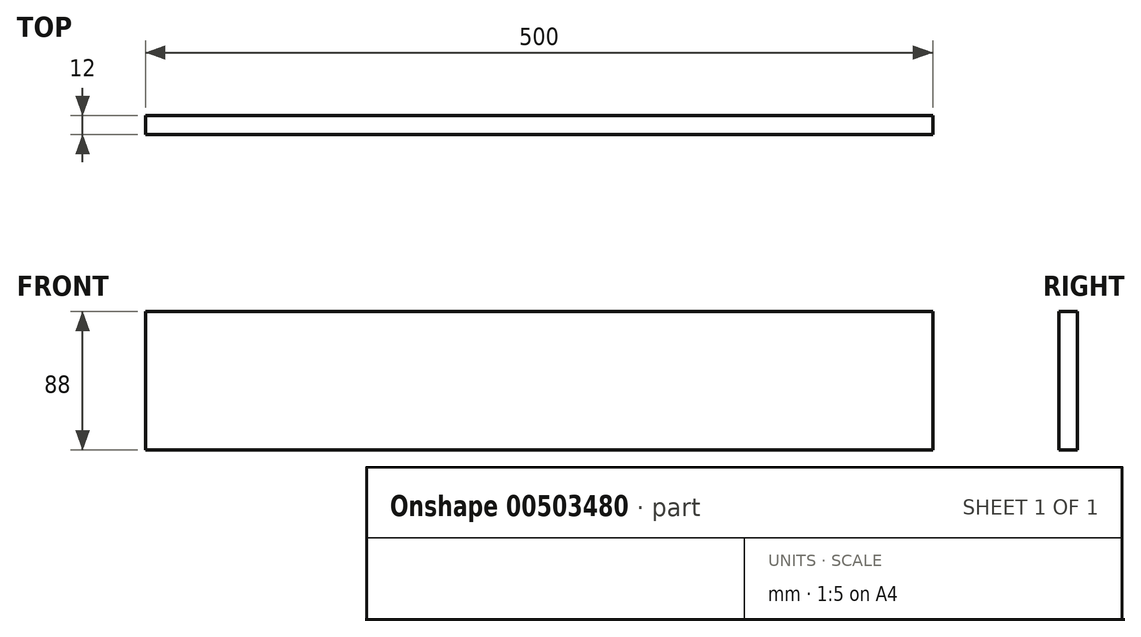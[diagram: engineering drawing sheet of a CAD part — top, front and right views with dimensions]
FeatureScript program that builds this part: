
annotation { "Feature Type Name" : "Feature", "Feature Type Description" : "" }
export const myFeature = defineFeature(function(context is Context, id is Id, definition is map)
    precondition{}
    {
        {
            var Q0;
            Q0=qCreatedBy(makeId("Top.planeOp"),FACE);
            var sketch = newSketch(context, id + "F0", { "sketchPlane" : qUnion([Q0])});
            skLineSegment(sketch, "E0.bottom", {"start": v(250, -250) * mm, "end": v(-250, -250) * mm});
            skLineSegment(sketch, "E0.top", {"start": v(250, 250) * mm, "end": v(-250, 250) * mm});
            skLineSegment(sketch, "E0.left", {"start": v(250, -250) * mm, "end": v(250, 250) * mm});
            skLineSegment(sketch, "E0.right", {"start": v(-250, -250) * mm, "end": v(-250, 250) * mm});
            skPoint(sketch, "E0.middle", {"position": v(0, 0) * mm});
            skSolve(sketch);
        }
        {
            var Q0;
            Q0=qSketchRegion(id+"F0",true);
            extrude(context, id + "F1", {"entities" : qUnion([Q0]), "depth" : 12 * mm, "offsetDistance" : 25 * mm});
        }
        {
            var Q0;
            Q0=qCreatedBy(makeId("Right.planeOp"),FACE);
            var sketch = newSketch(context, id + "F2", { "sketchPlane" : qUnion([Q0])});
            skLineSegment(sketch, "E1.bottom", {"start": v(250, -25) * mm, "end": v(-250, -25) * mm});
            skLineSegment(sketch, "E1.top", {"start": v(250, 25) * mm, "end": v(-250, 25) * mm});
            skLineSegment(sketch, "E1.left", {"start": v(250, -25) * mm, "end": v(250, 25) * mm});
            skLineSegment(sketch, "E1.right", {"start": v(-250, -25) * mm, "end": v(-250, 25) * mm});
            skPoint(sketch, "E1.middle", {"position": v(0, 0) * mm});
            skSolve(sketch);
        }
        {
            var Q0;
            Q0=qSketchRegion(id+"F2",true);
            extrude(context, id + "F3", {"entities" : qUnion([Q0]), "endBound" : BoundingType.SYMMETRIC, "depth" : 12 * mm, "offsetDistance" : 25 * mm});
        }
        {
            var Q0;
            Q0=makeQuery(id+"F3.opExtrude","SWEPT_BODY",BODY,{"disambiguationData":[OSD([sQuery(id+"F2.wireOp",EDGE,"E1.bottom"),sQuery(id+"F2.wireOp",EDGE,"E1.top"),sQuery(id+"F2.wireOp",EDGE,"E1.left"),sQuery(id+"F2.wireOp",EDGE,"E1.right")])]});
            transform(context, id + "F4", {"entities" : qUnion([Q0]), "transformType" : TransformType.TRANSLATION_3D, "dx" : 0 * mm, "dy" : 0 * mm, "dz" : -25 * mm, "makeCopy" : false});
        }
        {
            var Q0;
            Q0=qCreatedBy(makeId("Front.planeOp"),FACE);
            var sketch = newSketch(context, id + "F5", { "sketchPlane" : qUnion([Q0])});
            skLineSegment(sketch, "E2.bottom", {"start": v(250, -25) * mm, "end": v(-250, -25) * mm});
            skLineSegment(sketch, "E2.left", {"start": v(250, -25) * mm, "end": v(250, 25) * mm});
            skLineSegment(sketch, "E2.right", {"start": v(-250, -25) * mm, "end": v(-250, 25) * mm});
            skPoint(sketch, "E2.middle", {"position": v(0, 0) * mm});
            skLineSegment(sketch, "E3", {"start": v(-250, 25) * mm, "end": v(-6, 25) * mm});
            skLineSegment(sketch, "E4", {"start": v(-6, 25) * mm, "end": v(-6, 0) * mm});
            skLineSegment(sketch, "E5", {"start": v(-6, 0) * mm, "end": v(6, 0) * mm});
            skLineSegment(sketch, "E6", {"start": v(6, 0) * mm, "end": v(6, 25) * mm});
            skLineSegment(sketch, "E7", {"start": v(6, 25) * mm, "end": v(250, 25) * mm});
            skSolve(sketch);
        }
        {
            var Q0;
            Q0=qSketchRegion(id+"F5",true);
            extrude(context, id + "F6", {"entities" : qUnion([Q0]), "endBound" : BoundingType.SYMMETRIC, "depth" : 12 * mm, "offsetDistance" : 25 * mm});
        }
        {
            var Q0;
            Q0=makeQuery(id+"F6.opExtrude","SWEPT_BODY",BODY,{"disambiguationData":[OSD([sQuery(id+"F5.wireOp",EDGE,"E2.bottom"),sQuery(id+"F5.wireOp",EDGE,"E2.top"),sQuery(id+"F5.wireOp",EDGE,"E2.left"),sQuery(id+"F5.wireOp",EDGE,"E2.right")])]});
            transform(context, id + "F7", {"entities" : qUnion([Q0]), "transformType" : TransformType.TRANSLATION_3D, "dx" : 0 * mm, "dy" : 80 * mm, "dz" : -25 * mm, "makeCopy" : false});
        }
        {
            var Q0;
            Q0=makeQuery(id+"F6.opExtrude","SWEPT_BODY",BODY,{"disambiguationData":[OSD([sQuery(id+"F5.wireOp",EDGE,"E2.bottom"),sQuery(id+"F5.wireOp",EDGE,"E2.top"),sQuery(id+"F5.wireOp",EDGE,"E2.left"),sQuery(id+"F5.wireOp",EDGE,"E2.right")])]});
            transform(context, id + "F8", {"entities" : qUnion([Q0]), "transformType" : TransformType.COPY});
        }
        {
            var Q0;
            Q0=makeQuery(id+"F8.opPattern","COPY",BODY,{"derivedFrom":makeQuery(id+"F6.opExtrude","SWEPT_BODY",BODY,{"disambiguationData":[OSD([sQuery(id+"F5.wireOp",EDGE,"E2.bottom"),sQuery(id+"F5.wireOp",EDGE,"E2.top"),sQuery(id+"F5.wireOp",EDGE,"E2.left"),sQuery(id+"F5.wireOp",EDGE,"E2.right")])]}),"instanceName":"1"});
            deleteBodies(context, id + "F9", {"entities" : qUnion([Q0])});
        }
        {
            var Q0;
            Q0=makeQuery(id+"F6.opExtrude","SWEPT_BODY",BODY,{"disambiguationData":[OSD([sQuery(id+"F5.wireOp",EDGE,"E2.bottom"),sQuery(id+"F5.wireOp",EDGE,"E2.left"),sQuery(id+"F5.wireOp",EDGE,"E2.right"),sQuery(id+"F5.wireOp",EDGE,"E3"),sQuery(id+"F5.wireOp",EDGE,"E4"),sQuery(id+"F5.wireOp",EDGE,"E5"),sQuery(id+"F5.wireOp",EDGE,"E6"),sQuery(id+"F5.wireOp",EDGE,"E7")])]});
            var Q1;
            Q1=makeQuery(id+"F3.opExtrude","SWEPT_BODY",BODY,{"disambiguationData":[OSD([sQuery(id+"F2.wireOp",EDGE,"E1.bottom"),sQuery(id+"F2.wireOp",EDGE,"E1.top"),sQuery(id+"F2.wireOp",EDGE,"E1.left"),sQuery(id+"F2.wireOp",EDGE,"E1.right")])]});
            booleanBodies(context, id + "F10", {"operationType" : BooleanOperationType.SUBTRACTION, "tools" : qUnion([Q0]), "targets" : qUnion([Q1]), "keepTools" : true});
        }
        {
            var Q0;
            Q0=makeQuery(id+"F6.opExtrude","SWEPT_BODY",BODY,{"disambiguationData":[OSD([sQuery(id+"F5.wireOp",EDGE,"E2.bottom"),sQuery(id+"F5.wireOp",EDGE,"E2.left"),sQuery(id+"F5.wireOp",EDGE,"E2.right"),sQuery(id+"F5.wireOp",EDGE,"E3"),sQuery(id+"F5.wireOp",EDGE,"E4"),sQuery(id+"F5.wireOp",EDGE,"E5"),sQuery(id+"F5.wireOp",EDGE,"E6"),sQuery(id+"F5.wireOp",EDGE,"E7")])]});
            transform(context, id + "F11", {"entities" : qUnion([Q0]), "transformType" : TransformType.TRANSLATION_3D, "dx" : 0 * mm, "dy" : 164 * mm, "dz" : 0 * mm, "makeCopy" : true});
        }
        {
            var Q0;
            Q0=makeQuery(id+"F11.opPattern","COPY",BODY,{"derivedFrom":makeQuery(id+"F6.opExtrude","SWEPT_BODY",BODY,{"disambiguationData":[OSD([sQuery(id+"F5.wireOp",EDGE,"E2.bottom"),sQuery(id+"F5.wireOp",EDGE,"E2.left"),sQuery(id+"F5.wireOp",EDGE,"E2.right"),sQuery(id+"F5.wireOp",EDGE,"E3"),sQuery(id+"F5.wireOp",EDGE,"E4"),sQuery(id+"F5.wireOp",EDGE,"E5"),sQuery(id+"F5.wireOp",EDGE,"E6"),sQuery(id+"F5.wireOp",EDGE,"E7")])]}),"instanceName":"1"});
            var Q1;
            Q1=makeQuery(id+"F3.opExtrude","SWEPT_BODY",BODY,{"disambiguationData":[OSD([sQuery(id+"F2.wireOp",EDGE,"E1.bottom"),sQuery(id+"F2.wireOp",EDGE,"E1.top"),sQuery(id+"F2.wireOp",EDGE,"E1.left"),sQuery(id+"F2.wireOp",EDGE,"E1.right")])]});
            booleanBodies(context, id + "F12", {"operationType" : BooleanOperationType.SUBTRACTION, "tools" : qUnion([Q0]), "targets" : qUnion([Q1]), "keepTools" : true});
        }
        {
            var Q0;
            Q0=qCreatedBy(makeId("Right.planeOp"),FACE);
            var sketch = newSketch(context, id + "F13", { "sketchPlane" : qUnion([Q0])});
            skLineSegment(sketch, "E8", {"start": v(0, 0) * mm, "end": v(250, 0) * mm});
            skLineSegment(sketch, "E9", {"start": v(250, 0) * mm, "end": v(250, -50) * mm});
            skLineSegment(sketch, "E10", {"start": v(250, -50) * mm, "end": v(-250, -50) * mm});
            skLineSegment(sketch, "E11", {"start": v(-250, -50) * mm, "end": v(-250, 100) * mm});
            skLineSegment(sketch, "E12", {"start": v(250, 0) * mm, "end": v(250, 452) * mm});
            skLineSegment(sketch, "E13", {"start": v(250, 452) * mm, "end": v(-110, 452) * mm});
            skLineSegment(sketch, "E14", {"start": v(-110, 452) * mm, "end": v(-250, 100) * mm});
            skLineSegment(sketch, "E15", {"start": v(250, 452) * mm, "end": v(70, 452) * mm});
            skLineSegment(sketch, "E16", {"start": v(70, 452) * mm, "end": v(70, 392) * mm});
            skLineSegment(sketch, "E17.bottom", {"start": v(140, 372) * mm, "end": v(0, 372) * mm});
            skLineSegment(sketch, "E17.top", {"start": v(140, 412) * mm, "end": v(0, 412) * mm});
            skLineSegment(sketch, "E17.left", {"start": v(140, 372) * mm, "end": v(140, 412) * mm});
            skLineSegment(sketch, "E17.right", {"start": v(0, 372) * mm, "end": v(0, 412) * mm});
            skPoint(sketch, "E17.middle", {"position": v(70, 392) * mm});
            skSolve(sketch);
        }
        {
            var Q0;
            Q0=makeQuery(id+"F13.imprint","IMPRINT",FACE,{"disambiguationData":[TD([[makeQuery(id+"F13.imprint","IMPRINT",EDGE,{"derivedFrom":sQuery(id+"F13.wireOp",EDGE,"E9")}),-1.0]])]});
            extrude(context, id + "F14", {"entities" : qUnion([Q0]), "endBound" : BoundingType.SYMMETRIC, "depth" : 12 * mm, "offsetDistance" : 25 * mm});
        }
        {
            var Q0;
            Q0=makeQuery(id+"F14.opExtrude","SWEPT_EDGE",EDGE,{"disambiguationData":[OSD([sQuery(id+"F13.wireOp",EDGE,"E17.bottom"),sQuery(id+"F13.wireOp",EDGE,"E17.left")])]});
            var Q1;
            Q1=makeQuery(id+"F14.opExtrude","SWEPT_EDGE",EDGE,{"disambiguationData":[OSD([sQuery(id+"F13.wireOp",EDGE,"E17.top"),sQuery(id+"F13.wireOp",EDGE,"E17.left")])]});
            var Q2;
            Q2=makeQuery(id+"F14.opExtrude","SWEPT_EDGE",EDGE,{"disambiguationData":[OSD([sQuery(id+"F13.wireOp",EDGE,"E17.top"),sQuery(id+"F13.wireOp",EDGE,"E17.right")])]});
            var Q3;
            Q3=makeQuery(id+"F14.opExtrude","SWEPT_EDGE",EDGE,{"disambiguationData":[OSD([sQuery(id+"F13.wireOp",EDGE,"E17.bottom"),sQuery(id+"F13.wireOp",EDGE,"E17.right")])]});
            fillet(context, id + "F15", {"entities" : qUnion([Q0, Q1, Q2, Q3]), "radius" : 20 * mm, "tangentPropagation" : true, "allowEdgeOverflow" : false});
        }
        {
            var Q0;
            Q0=makeQuery(id+"F14.opExtrude","SWEPT_BODY",BODY,{"disambiguationData":[OSD([sQuery(id+"F13.wireOp",EDGE,"E9"),sQuery(id+"F13.wireOp",EDGE,"E10"),sQuery(id+"F13.wireOp",EDGE,"E11"),sQuery(id+"F13.wireOp",EDGE,"E12"),sQuery(id+"F13.wireOp",EDGE,"E13"),sQuery(id+"F13.wireOp",EDGE,"E14"),sQuery(id+"F13.wireOp",EDGE,"E17.bottom"),sQuery(id+"F13.wireOp",EDGE,"E17.top"),sQuery(id+"F13.wireOp",EDGE,"E17.left"),sQuery(id+"F13.wireOp",EDGE,"E17.right")])]});
            transform(context, id + "F16", {"entities" : qUnion([Q0]), "transformType" : TransformType.TRANSLATION_3D, "dx" : -256 * mm, "dy" : 0 * mm, "dz" : 0 * mm, "makeCopy" : false});
        }
        {
            var Q0;
            Q0=makeQuery(id+"F14.opExtrude","SWEPT_BODY",BODY,{"disambiguationData":[OSD([sQuery(id+"F13.wireOp",EDGE,"E9"),sQuery(id+"F13.wireOp",EDGE,"E10"),sQuery(id+"F13.wireOp",EDGE,"E11"),sQuery(id+"F13.wireOp",EDGE,"E12"),sQuery(id+"F13.wireOp",EDGE,"E13"),sQuery(id+"F13.wireOp",EDGE,"E14"),sQuery(id+"F13.wireOp",EDGE,"E17.bottom"),sQuery(id+"F13.wireOp",EDGE,"E17.top"),sQuery(id+"F13.wireOp",EDGE,"E17.left"),sQuery(id+"F13.wireOp",EDGE,"E17.right")])]});
            transform(context, id + "F17", {"entities" : qUnion([Q0]), "transformType" : TransformType.TRANSLATION_3D, "dx" : 512 * mm, "dy" : 0 * mm, "dz" : 0 * mm, "makeCopy" : true});
        }
        {
            var Q0;
            Q0=qCreatedBy(makeId("Front.planeOp"),FACE);
            var sketch = newSketch(context, id + "F18", { "sketchPlane" : qUnion([Q0])});
            skLineSegment(sketch, "E18", {"start": v(0, 0) * mm, "end": v(-262, 0) * mm});
            skLineSegment(sketch, "E19", {"start": v(-262, 0) * mm, "end": v(-262, -50) * mm});
            skLineSegment(sketch, "E20", {"start": v(-262, -50) * mm, "end": v(262, -50) * mm});
            skLineSegment(sketch, "E21", {"start": v(262, -50) * mm, "end": v(262, 452) * mm});
            skLineSegment(sketch, "E22", {"start": v(262, 452) * mm, "end": v(-262, 452) * mm});
            skLineSegment(sketch, "E23", {"start": v(-262, 452) * mm, "end": v(-262, 0) * mm});
            skSolve(sketch);
        }
        {
            var Q0;
            Q0=qSketchRegion(id+"F18",true);
            extrude(context, id + "F19", {"entities" : qUnion([Q0]), "endBound" : BoundingType.SYMMETRIC, "depth" : 12 * mm, "offsetDistance" : 25 * mm});
        }
        {
            var Q0;
            Q0=makeQuery(id+"F19.opExtrude","SWEPT_BODY",BODY,{"disambiguationData":[OSD([sQuery(id+"F18.wireOp",EDGE,"E19"),sQuery(id+"F18.wireOp",EDGE,"E20"),sQuery(id+"F18.wireOp",EDGE,"E21"),sQuery(id+"F18.wireOp",EDGE,"E22"),sQuery(id+"F18.wireOp",EDGE,"E23")])]});
            transform(context, id + "F20", {"entities" : qUnion([Q0]), "transformType" : TransformType.TRANSLATION_3D, "dx" : 0 * mm, "dy" : 256 * mm, "dz" : 0 * mm, "makeCopy" : false});
        }
        {
            var Q0;
            Q0=makeQuery(id+"F1.opExtrude","CAP_FACE",FACE,{"disambiguationData":[OSD([sQuery(id+"F0.wireOp",EDGE,"E0.bottom"),sQuery(id+"F0.wireOp",EDGE,"E0.top"),sQuery(id+"F0.wireOp",EDGE,"E0.left"),sQuery(id+"F0.wireOp",EDGE,"E0.right")])],"isStart":false});
            var sketch = newSketch(context, id + "F21", { "sketchPlane" : qUnion([Q0])});
            skLineSegment(sketch, "E24", {"start": v(0, 0) * mm, "end": v(0, 262) * mm});
            skLineSegment(sketch, "E25", {"start": v(0, 262) * mm, "end": v(262, 262) * mm});
            skLineSegment(sketch, "E26", {"start": v(262, 262) * mm, "end": v(262, -110) * mm});
            skLineSegment(sketch, "E27", {"start": v(262, -110) * mm, "end": v(-262, -110) * mm});
            skLineSegment(sketch, "E28", {"start": v(-262, -110) * mm, "end": v(-262, 262) * mm});
            skLineSegment(sketch, "E29", {"start": v(-262, 262) * mm, "end": v(0, 262) * mm});
            skSolve(sketch);
        }
        {
            var Q0;
            Q0=qSketchRegion(id+"F21",true);
            extrude(context, id + "F22", {"entities" : qUnion([Q0]), "depth" : 12 * mm, "offsetDistance" : 25 * mm});
        }
        {
            var Q0;
            Q0=makeQuery(id+"F22.opExtrude","SWEPT_BODY",BODY,{"disambiguationData":[OSD([sQuery(id+"F21.wireOp",EDGE,"E25"),sQuery(id+"F21.wireOp",EDGE,"E26"),sQuery(id+"F21.wireOp",EDGE,"E27"),sQuery(id+"F21.wireOp",EDGE,"E28"),sQuery(id+"F21.wireOp",EDGE,"E29")])]});
            transform(context, id + "F23", {"entities" : qUnion([Q0]), "transformType" : TransformType.TRANSLATION_3D, "dx" : 0 * mm, "dy" : 0 * mm, "dz" : 440 * mm, "makeCopy" : false});
        }
        {
            var Q0;
            Q0=qCreatedBy(makeId("Front.planeOp"),FACE);
            var sketch = newSketch(context, id + "F24", { "sketchPlane" : qUnion([Q0])});
            skLineSegment(sketch, "E30", {"start": v(0, 0) * mm, "end": v(0, 12) * mm});
            skLineSegment(sketch, "E31", {"start": v(0, 12) * mm, "end": v(250, 12) * mm});
            skLineSegment(sketch, "E32", {"start": v(250, 12) * mm, "end": v(250, 100) * mm});
            skLineSegment(sketch, "E33", {"start": v(250, 100) * mm, "end": v(-250, 100) * mm});
            skLineSegment(sketch, "E34", {"start": v(-250, 100) * mm, "end": v(-250, 12) * mm});
            skLineSegment(sketch, "E35", {"start": v(-250, 12) * mm, "end": v(0, 12) * mm});
            skSolve(sketch);
        }
        {
            var Q0;
            Q0=qSketchRegion(id+"F24",true);
            extrude(context, id + "F25", {"entities" : qUnion([Q0]), "endBound" : BoundingType.SYMMETRIC, "depth" : 12 * mm, "offsetDistance" : 25 * mm});
        }
        {
            var Q0;
            Q0=makeQuery(id+"F25.opExtrude","SWEPT_BODY",BODY,{"disambiguationData":[OSD([sQuery(id+"F24.wireOp",EDGE,"E31"),sQuery(id+"F24.wireOp",EDGE,"E32"),sQuery(id+"F24.wireOp",EDGE,"E33"),sQuery(id+"F24.wireOp",EDGE,"E34"),sQuery(id+"F24.wireOp",EDGE,"E35")])]});
            transform(context, id + "F26", {"entities" : qUnion([Q0]), "transformType" : TransformType.TRANSLATION_3D, "dx" : 0 * mm, "dy" : -244 * mm, "dz" : 0 * mm, "makeCopy" : false});
        }
        {
            var Q0;
            Q0=qCreatedBy(makeId("Top.planeOp"),FACE);
            var sketch = newSketch(context, id + "F27", { "sketchPlane" : qUnion([Q0])});
            skLineSegment(sketch, "E36", {"start": v(0, 0) * mm, "end": v(0, 70) * mm});
            skLineSegment(sketch, "E37", {"start": v(0, 70) * mm, "end": v(-18, 70) * mm});
            skLineSegment(sketch, "E38", {"start": v(-18, 70) * mm, "end": v(-18, -250) * mm});
            skLineSegment(sketch, "E39", {"start": v(-18, -250) * mm, "end": v(-30, -250) * mm});
            skLineSegment(sketch, "E40", {"start": v(-30, -250) * mm, "end": v(-30, 70) * mm});
            skLineSegment(sketch, "E41", {"start": v(-30, 70) * mm, "end": v(-18, 70) * mm});
            skSolve(sketch);
        }
        {
            var Q0;
            Q0=qSketchRegion(id+"F27",true);
            extrude(context, id + "F28", {"entities" : qUnion([Q0]), "depth" : 44 * mm, "offsetDistance" : 25 * mm});
        }
        {
            var Q0;
            Q0=makeQuery(id+"F28.opExtrude","SWEPT_BODY",BODY,{"disambiguationData":[OSD([sQuery(id+"F27.wireOp",EDGE,"E38"),sQuery(id+"F27.wireOp",EDGE,"E39"),sQuery(id+"F27.wireOp",EDGE,"E40"),sQuery(id+"F27.wireOp",EDGE,"E41")])]});
            transform(context, id + "F29", {"entities" : qUnion([Q0]), "transformType" : TransformType.TRANSLATION_3D, "dx" : 0 * mm, "dy" : 0 * mm, "dz" : -48 * mm, "makeCopy" : false});
        }
        {
            var Q0;
            Q0=makeQuery(id+"F28.opExtrude","SWEPT_BODY",BODY,{"disambiguationData":[OSD([sQuery(id+"F27.wireOp",EDGE,"E38"),sQuery(id+"F27.wireOp",EDGE,"E39"),sQuery(id+"F27.wireOp",EDGE,"E40"),sQuery(id+"F27.wireOp",EDGE,"E41")])]});
            transform(context, id + "F30", {"entities" : qUnion([Q0]), "transformType" : TransformType.TRANSLATION_3D, "dx" : -208 * mm, "dy" : 0 * mm, "dz" : 0 * mm, "makeCopy" : true});
        }
        {
            var Q0;
            Q0=qCreatedBy(makeId("Top.planeOp"),FACE);
            var sketch = newSketch(context, id + "F31", { "sketchPlane" : qUnion([Q0])});
            skLineSegment(sketch, "E42", {"start": v(0, 0) * mm, "end": v(0, -250) * mm});
            skLineSegment(sketch, "E43", {"start": v(0, -250) * mm, "end": v(-30, -250) * mm});
            skLineSegment(sketch, "E44", {"start": v(-30, -250) * mm, "end": v(-226, -250) * mm});
            skLineSegment(sketch, "E45", {"start": v(-226, -250) * mm, "end": v(-226, -238) * mm});
            skLineSegment(sketch, "E46", {"start": v(-226, -238) * mm, "end": v(-30, -238) * mm});
            skLineSegment(sketch, "E47", {"start": v(-30, -238) * mm, "end": v(-30, -250) * mm});
            skSolve(sketch);
        }
        {
            var Q0;
            Q0=qSketchRegion(id+"F31",true);
            extrude(context, id + "F32", {"entities" : qUnion([Q0]), "depth" : -44 * mm, "offsetDistance" : 25 * mm});
        }
        {
            var Q0;
            Q0=makeQuery(id+"F32.opExtrude","SWEPT_BODY",BODY,{"disambiguationData":[OSD([sQuery(id+"F31.wireOp",EDGE,"E44"),sQuery(id+"F31.wireOp",EDGE,"E45"),sQuery(id+"F31.wireOp",EDGE,"E46"),sQuery(id+"F31.wireOp",EDGE,"E47")])]});
            transform(context, id + "F33", {"entities" : qUnion([Q0]), "transformType" : TransformType.TRANSLATION_3D, "dx" : 0 * mm, "dy" : 0 * mm, "dz" : -4 * mm, "makeCopy" : false});
        }
        {
            var Q0;
            Q0=makeQuery(id+"F32.opExtrude","SWEPT_BODY",BODY,{"disambiguationData":[OSD([sQuery(id+"F31.wireOp",EDGE,"E44"),sQuery(id+"F31.wireOp",EDGE,"E45"),sQuery(id+"F31.wireOp",EDGE,"E46"),sQuery(id+"F31.wireOp",EDGE,"E47")])]});
            transform(context, id + "F34", {"entities" : qUnion([Q0]), "transformType" : TransformType.TRANSLATION_3D, "dx" : 0 * mm, "dy" : 308 * mm, "dz" : 0 * mm, "makeCopy" : true});
        }
        {
            var Q0;
            Q0=makeQuery(id+"F32.opExtrude","SWEPT_BODY",BODY,{"disambiguationData":[OSD([sQuery(id+"F31.wireOp",EDGE,"E44"),sQuery(id+"F31.wireOp",EDGE,"E45"),sQuery(id+"F31.wireOp",EDGE,"E46"),sQuery(id+"F31.wireOp",EDGE,"E47")])]});
            var Q1;
            Q1=makeQuery(id+"F30.opPattern","COPY",BODY,{"derivedFrom":makeQuery(id+"F28.opExtrude","SWEPT_BODY",BODY,{"disambiguationData":[OSD([sQuery(id+"F27.wireOp",EDGE,"E38"),sQuery(id+"F27.wireOp",EDGE,"E39"),sQuery(id+"F27.wireOp",EDGE,"E40"),sQuery(id+"F27.wireOp",EDGE,"E41")])]}),"instanceName":"1"});
            var Q2;
            Q2=makeQuery(id+"F28.opExtrude","SWEPT_BODY",BODY,{"disambiguationData":[OSD([sQuery(id+"F27.wireOp",EDGE,"E38"),sQuery(id+"F27.wireOp",EDGE,"E39"),sQuery(id+"F27.wireOp",EDGE,"E40"),sQuery(id+"F27.wireOp",EDGE,"E41")])]});
            var Q3;
            Q3=makeQuery(id+"F34.opPattern","COPY",BODY,{"derivedFrom":makeQuery(id+"F32.opExtrude","SWEPT_BODY",BODY,{"disambiguationData":[OSD([sQuery(id+"F31.wireOp",EDGE,"E44"),sQuery(id+"F31.wireOp",EDGE,"E45"),sQuery(id+"F31.wireOp",EDGE,"E46"),sQuery(id+"F31.wireOp",EDGE,"E47")])]}),"instanceName":"1"});
            transform(context, id + "F35", {"entities" : qUnion([Q0, Q1, Q2, Q3]), "transformType" : TransformType.TRANSLATION_3D, "dx" : 256 * mm, "dy" : 0 * mm, "dz" : 0 * mm, "makeCopy" : true});
        }
        {
            var Q0;
            Q0=qCreatedBy(makeId("Top.planeOp"),FACE);
            var sketch = newSketch(context, id + "F36", { "sketchPlane" : qUnion([Q0])});
            skLineSegment(sketch, "E48", {"start": v(0, 0) * mm, "end": v(-24, 0) * mm});
            skLineSegment(sketch, "E49", {"start": v(-24, 0) * mm, "end": v(-24, -244) * mm});
            skLineSegment(sketch, "E50", {"start": v(-24, -244) * mm, "end": v(-232, -244) * mm});
            skLineSegment(sketch, "E51", {"start": v(-232, -244) * mm, "end": v(-232, 64) * mm});
            skLineSegment(sketch, "E52", {"start": v(-232, 64) * mm, "end": v(-24, 64) * mm});
            skLineSegment(sketch, "E53", {"start": v(-24, 64) * mm, "end": v(-24, 0) * mm});
            skSolve(sketch);
        }
        {
            var Q0;
            Q0=qSketchRegion(id+"F36",true);
            extrude(context, id + "F37", {"entities" : qUnion([Q0]), "depth" : 3 * mm, "offsetDistance" : 25 * mm});
        }
        {
            var Q0;
            Q0=makeQuery(id+"F37.opExtrude","SWEPT_BODY",BODY,{"disambiguationData":[OSD([sQuery(id+"F36.wireOp",EDGE,"E49"),sQuery(id+"F36.wireOp",EDGE,"E50"),sQuery(id+"F36.wireOp",EDGE,"E51"),sQuery(id+"F36.wireOp",EDGE,"E52"),sQuery(id+"F36.wireOp",EDGE,"E53")])]});
            transform(context, id + "F38", {"entities" : qUnion([Q0]), "transformType" : TransformType.TRANSLATION_3D, "dx" : 0 * mm, "dy" : 0 * mm, "dz" : -44 * mm, "makeCopy" : false});
        }
        {
            var Q0;
            Q0=makeQuery(id+"F37.opExtrude","SWEPT_BODY",BODY,{"disambiguationData":[OSD([sQuery(id+"F36.wireOp",EDGE,"E49"),sQuery(id+"F36.wireOp",EDGE,"E50"),sQuery(id+"F36.wireOp",EDGE,"E51"),sQuery(id+"F36.wireOp",EDGE,"E52"),sQuery(id+"F36.wireOp",EDGE,"E53")])]});
            transform(context, id + "F39", {"entities" : qUnion([Q0]), "transformType" : TransformType.TRANSLATION_3D, "dx" : 256 * mm, "dy" : 0 * mm, "dz" : 0 * mm, "makeCopy" : true});
        }
        {
            var Q0;
            Q0=makeQuery(id+"F37.opExtrude","SWEPT_BODY",BODY,{"disambiguationData":[OSD([sQuery(id+"F36.wireOp",EDGE,"E49"),sQuery(id+"F36.wireOp",EDGE,"E50"),sQuery(id+"F36.wireOp",EDGE,"E51"),sQuery(id+"F36.wireOp",EDGE,"E52"),sQuery(id+"F36.wireOp",EDGE,"E53")])]});
            var Q1;
            Q1=makeQuery(id+"F30.opPattern","COPY",BODY,{"derivedFrom":makeQuery(id+"F28.opExtrude","SWEPT_BODY",BODY,{"disambiguationData":[OSD([sQuery(id+"F27.wireOp",EDGE,"E38"),sQuery(id+"F27.wireOp",EDGE,"E39"),sQuery(id+"F27.wireOp",EDGE,"E40"),sQuery(id+"F27.wireOp",EDGE,"E41")])]}),"instanceName":"1"});
            var Q2;
            Q2=makeQuery(id+"F32.opExtrude","SWEPT_BODY",BODY,{"disambiguationData":[OSD([sQuery(id+"F31.wireOp",EDGE,"E44"),sQuery(id+"F31.wireOp",EDGE,"E45"),sQuery(id+"F31.wireOp",EDGE,"E46"),sQuery(id+"F31.wireOp",EDGE,"E47")])]});
            var Q3;
            Q3=makeQuery(id+"F28.opExtrude","SWEPT_BODY",BODY,{"disambiguationData":[OSD([sQuery(id+"F27.wireOp",EDGE,"E38"),sQuery(id+"F27.wireOp",EDGE,"E39"),sQuery(id+"F27.wireOp",EDGE,"E40"),sQuery(id+"F27.wireOp",EDGE,"E41")])]});
            var Q4;
            Q4=makeQuery(id+"F34.opPattern","COPY",BODY,{"derivedFrom":makeQuery(id+"F32.opExtrude","SWEPT_BODY",BODY,{"disambiguationData":[OSD([sQuery(id+"F31.wireOp",EDGE,"E44"),sQuery(id+"F31.wireOp",EDGE,"E45"),sQuery(id+"F31.wireOp",EDGE,"E46"),sQuery(id+"F31.wireOp",EDGE,"E47")])]}),"instanceName":"1"});
            booleanBodies(context, id + "F40", {"operationType" : BooleanOperationType.SUBTRACTION, "tools" : qUnion([Q0]), "targets" : qUnion([Q1, Q2, Q3, Q4]), "keepTools" : true});
        }
        {
            var Q0;
            Q0=makeQuery(id+"F39.opPattern","COPY",BODY,{"derivedFrom":makeQuery(id+"F37.opExtrude","SWEPT_BODY",BODY,{"disambiguationData":[OSD([sQuery(id+"F36.wireOp",EDGE,"E49"),sQuery(id+"F36.wireOp",EDGE,"E50"),sQuery(id+"F36.wireOp",EDGE,"E51"),sQuery(id+"F36.wireOp",EDGE,"E52"),sQuery(id+"F36.wireOp",EDGE,"E53")])]}),"instanceName":"1"});
            var Q1;
            Q1=makeQuery(id+"F35.opPattern","COPY",BODY,{"derivedFrom":makeQuery(id+"F32.opExtrude","SWEPT_BODY",BODY,{"disambiguationData":[OSD([sQuery(id+"F31.wireOp",EDGE,"E44"),sQuery(id+"F31.wireOp",EDGE,"E45"),sQuery(id+"F31.wireOp",EDGE,"E46"),sQuery(id+"F31.wireOp",EDGE,"E47")])]}),"instanceName":"1"});
            var Q2;
            Q2=makeQuery(id+"F35.opPattern","COPY",BODY,{"derivedFrom":makeQuery(id+"F28.opExtrude","SWEPT_BODY",BODY,{"disambiguationData":[OSD([sQuery(id+"F27.wireOp",EDGE,"E38"),sQuery(id+"F27.wireOp",EDGE,"E39"),sQuery(id+"F27.wireOp",EDGE,"E40"),sQuery(id+"F27.wireOp",EDGE,"E41")])]}),"instanceName":"1"});
            var Q3;
            Q3=makeQuery(id+"F35.opPattern","COPY",BODY,{"derivedFrom":makeQuery(id+"F34.opPattern","COPY",BODY,{"derivedFrom":makeQuery(id+"F32.opExtrude","SWEPT_BODY",BODY,{"disambiguationData":[OSD([sQuery(id+"F31.wireOp",EDGE,"E44"),sQuery(id+"F31.wireOp",EDGE,"E45"),sQuery(id+"F31.wireOp",EDGE,"E46"),sQuery(id+"F31.wireOp",EDGE,"E47")])]}),"instanceName":"1"}),"instanceName":"1"});
            var Q4;
            Q4=makeQuery(id+"F35.opPattern","COPY",BODY,{"derivedFrom":makeQuery(id+"F30.opPattern","COPY",BODY,{"derivedFrom":makeQuery(id+"F28.opExtrude","SWEPT_BODY",BODY,{"disambiguationData":[OSD([sQuery(id+"F27.wireOp",EDGE,"E38"),sQuery(id+"F27.wireOp",EDGE,"E39"),sQuery(id+"F27.wireOp",EDGE,"E40"),sQuery(id+"F27.wireOp",EDGE,"E41")])]}),"instanceName":"1"}),"instanceName":"1"});
            booleanBodies(context, id + "F41", {"operationType" : BooleanOperationType.SUBTRACTION, "tools" : qUnion([Q0]), "targets" : qUnion([Q1, Q2, Q3, Q4]), "keepTools" : true});
        }
        {
            var Q0;
            Q0=qCreatedBy(makeId("Front.planeOp"),FACE);
            var sketch = newSketch(context, id + "F42", { "sketchPlane" : qUnion([Q0])});
            skLineSegment(sketch, "E54", {"start": v(0, 0) * mm, "end": v(0, 12) * mm});
            skLineSegment(sketch, "E55", {"start": v(0, 12) * mm, "end": v(262, 12) * mm});
            skLineSegment(sketch, "E56", {"start": v(262, 12) * mm, "end": v(262, -50) * mm});
            skLineSegment(sketch, "E57", {"start": v(262, -50) * mm, "end": v(0, -50) * mm});
            skLineSegment(sketch, "E58", {"start": v(0, -50) * mm, "end": v(0, 0) * mm});
            skSolve(sketch);
        }
        {
            var Q0;
            Q0=qSketchRegion(id+"F42",true);
            extrude(context, id + "F43", {"entities" : qUnion([Q0]), "depth" : 12 * mm, "offsetDistance" : 25 * mm});
        }
        {
            var Q0;
            Q0=makeQuery(id+"F43.opExtrude","SWEPT_BODY",BODY,{"disambiguationData":[OSD([sQuery(id+"F42.wireOp",EDGE,"E54"),sQuery(id+"F42.wireOp",EDGE,"E55"),sQuery(id+"F42.wireOp",EDGE,"E56"),sQuery(id+"F42.wireOp",EDGE,"E57"),sQuery(id+"F42.wireOp",EDGE,"E58")])]});
            transform(context, id + "F44", {"entities" : qUnion([Q0]), "transformType" : TransformType.TRANSLATION_3D, "dx" : 0 * mm, "dy" : -250 * mm, "dz" : 0 * mm, "makeCopy" : false});
        }
        {
            var Q0;
            Q0=makeQuery(id+"F43.opExtrude","SWEPT_BODY",BODY,{"disambiguationData":[OSD([sQuery(id+"F42.wireOp",EDGE,"E54"),sQuery(id+"F42.wireOp",EDGE,"E55"),sQuery(id+"F42.wireOp",EDGE,"E56"),sQuery(id+"F42.wireOp",EDGE,"E57"),sQuery(id+"F42.wireOp",EDGE,"E58")])]});
            transform(context, id + "F45", {"entities" : qUnion([Q0]), "transformType" : TransformType.TRANSLATION_3D, "dx" : -262 * mm, "dy" : 0 * mm, "dz" : 0 * mm, "makeCopy" : true});
        }
        {
            var Q0;
            Q0=makeQuery(id+"F19.opExtrude","SWEPT_BODY",BODY,{"disambiguationData":[OSD([sQuery(id+"F18.wireOp",EDGE,"E19"),sQuery(id+"F18.wireOp",EDGE,"E20"),sQuery(id+"F18.wireOp",EDGE,"E21"),sQuery(id+"F18.wireOp",EDGE,"E22"),sQuery(id+"F18.wireOp",EDGE,"E23")])]});
            var Q1;
            Q1=makeQuery(id+"F17.opPattern","COPY",BODY,{"derivedFrom":makeQuery(id+"F14.opExtrude","SWEPT_BODY",BODY,{"disambiguationData":[OSD([sQuery(id+"F13.wireOp",EDGE,"E9"),sQuery(id+"F13.wireOp",EDGE,"E10"),sQuery(id+"F13.wireOp",EDGE,"E11"),sQuery(id+"F13.wireOp",EDGE,"E12"),sQuery(id+"F13.wireOp",EDGE,"E13"),sQuery(id+"F13.wireOp",EDGE,"E14"),sQuery(id+"F13.wireOp",EDGE,"E17.bottom"),sQuery(id+"F13.wireOp",EDGE,"E17.top"),sQuery(id+"F13.wireOp",EDGE,"E17.left"),sQuery(id+"F13.wireOp",EDGE,"E17.right")])]}),"instanceName":"1"});
            var Q2;
            Q2=makeQuery(id+"F14.opExtrude","SWEPT_BODY",BODY,{"disambiguationData":[OSD([sQuery(id+"F13.wireOp",EDGE,"E9"),sQuery(id+"F13.wireOp",EDGE,"E10"),sQuery(id+"F13.wireOp",EDGE,"E11"),sQuery(id+"F13.wireOp",EDGE,"E12"),sQuery(id+"F13.wireOp",EDGE,"E13"),sQuery(id+"F13.wireOp",EDGE,"E14"),sQuery(id+"F13.wireOp",EDGE,"E17.bottom"),sQuery(id+"F13.wireOp",EDGE,"E17.top"),sQuery(id+"F13.wireOp",EDGE,"E17.left"),sQuery(id+"F13.wireOp",EDGE,"E17.right")])]});
            var Q3;
            Q3=makeQuery(id+"F11.opPattern","COPY",BODY,{"derivedFrom":makeQuery(id+"F6.opExtrude","SWEPT_BODY",BODY,{"disambiguationData":[OSD([sQuery(id+"F5.wireOp",EDGE,"E2.bottom"),sQuery(id+"F5.wireOp",EDGE,"E2.left"),sQuery(id+"F5.wireOp",EDGE,"E2.right"),sQuery(id+"F5.wireOp",EDGE,"E3"),sQuery(id+"F5.wireOp",EDGE,"E4"),sQuery(id+"F5.wireOp",EDGE,"E5"),sQuery(id+"F5.wireOp",EDGE,"E6"),sQuery(id+"F5.wireOp",EDGE,"E7")])]}),"instanceName":"1"});
            var Q4;
            Q4=makeQuery(id+"F6.opExtrude","SWEPT_BODY",BODY,{"disambiguationData":[OSD([sQuery(id+"F5.wireOp",EDGE,"E2.bottom"),sQuery(id+"F5.wireOp",EDGE,"E2.left"),sQuery(id+"F5.wireOp",EDGE,"E2.right"),sQuery(id+"F5.wireOp",EDGE,"E3"),sQuery(id+"F5.wireOp",EDGE,"E4"),sQuery(id+"F5.wireOp",EDGE,"E5"),sQuery(id+"F5.wireOp",EDGE,"E6"),sQuery(id+"F5.wireOp",EDGE,"E7")])]});
            var Q5;
            Q5=makeQuery(id+"F3.opExtrude","SWEPT_BODY",BODY,{"disambiguationData":[OSD([sQuery(id+"F2.wireOp",EDGE,"E1.bottom"),sQuery(id+"F2.wireOp",EDGE,"E1.top"),sQuery(id+"F2.wireOp",EDGE,"E1.left"),sQuery(id+"F2.wireOp",EDGE,"E1.right")])]});
            var Q6;
            Q6=makeQuery(id+"F1.opExtrude","SWEPT_BODY",BODY,{"disambiguationData":[OSD([sQuery(id+"F0.wireOp",EDGE,"E0.bottom"),sQuery(id+"F0.wireOp",EDGE,"E0.top"),sQuery(id+"F0.wireOp",EDGE,"E0.left"),sQuery(id+"F0.wireOp",EDGE,"E0.right")])]});
            var Q7;
            Q7=makeQuery(id+"F22.opExtrude","SWEPT_BODY",BODY,{"disambiguationData":[OSD([sQuery(id+"F21.wireOp",EDGE,"E25"),sQuery(id+"F21.wireOp",EDGE,"E26"),sQuery(id+"F21.wireOp",EDGE,"E27"),sQuery(id+"F21.wireOp",EDGE,"E28"),sQuery(id+"F21.wireOp",EDGE,"E29")])]});
            var Q8;
            Q8=makeQuery(id+"F28.opExtrude","SWEPT_BODY",BODY,{"disambiguationData":[OSD([sQuery(id+"F27.wireOp",EDGE,"E38"),sQuery(id+"F27.wireOp",EDGE,"E39"),sQuery(id+"F27.wireOp",EDGE,"E40"),sQuery(id+"F27.wireOp",EDGE,"E41")])]});
            var Q9;
            Q9=makeQuery(id+"F30.opPattern","COPY",BODY,{"derivedFrom":makeQuery(id+"F28.opExtrude","SWEPT_BODY",BODY,{"disambiguationData":[OSD([sQuery(id+"F27.wireOp",EDGE,"E38"),sQuery(id+"F27.wireOp",EDGE,"E39"),sQuery(id+"F27.wireOp",EDGE,"E40"),sQuery(id+"F27.wireOp",EDGE,"E41")])]}),"instanceName":"1"});
            var Q10;
            Q10=makeQuery(id+"F32.opExtrude","SWEPT_BODY",BODY,{"disambiguationData":[OSD([sQuery(id+"F31.wireOp",EDGE,"E44"),sQuery(id+"F31.wireOp",EDGE,"E45"),sQuery(id+"F31.wireOp",EDGE,"E46"),sQuery(id+"F31.wireOp",EDGE,"E47")])]});
            var Q11;
            Q11=makeQuery(id+"F34.opPattern","COPY",BODY,{"derivedFrom":makeQuery(id+"F32.opExtrude","SWEPT_BODY",BODY,{"disambiguationData":[OSD([sQuery(id+"F31.wireOp",EDGE,"E44"),sQuery(id+"F31.wireOp",EDGE,"E45"),sQuery(id+"F31.wireOp",EDGE,"E46"),sQuery(id+"F31.wireOp",EDGE,"E47")])]}),"instanceName":"1"});
            var Q12;
            Q12=makeQuery(id+"F35.opPattern","COPY",BODY,{"derivedFrom":makeQuery(id+"F28.opExtrude","SWEPT_BODY",BODY,{"disambiguationData":[OSD([sQuery(id+"F27.wireOp",EDGE,"E38"),sQuery(id+"F27.wireOp",EDGE,"E39"),sQuery(id+"F27.wireOp",EDGE,"E40"),sQuery(id+"F27.wireOp",EDGE,"E41")])]}),"instanceName":"1"});
            var Q13;
            Q13=makeQuery(id+"F35.opPattern","COPY",BODY,{"derivedFrom":makeQuery(id+"F30.opPattern","COPY",BODY,{"derivedFrom":makeQuery(id+"F28.opExtrude","SWEPT_BODY",BODY,{"disambiguationData":[OSD([sQuery(id+"F27.wireOp",EDGE,"E38"),sQuery(id+"F27.wireOp",EDGE,"E39"),sQuery(id+"F27.wireOp",EDGE,"E40"),sQuery(id+"F27.wireOp",EDGE,"E41")])]}),"instanceName":"1"}),"instanceName":"1"});
            var Q14;
            Q14=makeQuery(id+"F35.opPattern","COPY",BODY,{"derivedFrom":makeQuery(id+"F32.opExtrude","SWEPT_BODY",BODY,{"disambiguationData":[OSD([sQuery(id+"F31.wireOp",EDGE,"E44"),sQuery(id+"F31.wireOp",EDGE,"E45"),sQuery(id+"F31.wireOp",EDGE,"E46"),sQuery(id+"F31.wireOp",EDGE,"E47")])]}),"instanceName":"1"});
            var Q15;
            Q15=makeQuery(id+"F35.opPattern","COPY",BODY,{"derivedFrom":makeQuery(id+"F34.opPattern","COPY",BODY,{"derivedFrom":makeQuery(id+"F32.opExtrude","SWEPT_BODY",BODY,{"disambiguationData":[OSD([sQuery(id+"F31.wireOp",EDGE,"E44"),sQuery(id+"F31.wireOp",EDGE,"E45"),sQuery(id+"F31.wireOp",EDGE,"E46"),sQuery(id+"F31.wireOp",EDGE,"E47")])]}),"instanceName":"1"}),"instanceName":"1"});
            var Q16;
            Q16=makeQuery(id+"F37.opExtrude","SWEPT_BODY",BODY,{"disambiguationData":[OSD([sQuery(id+"F36.wireOp",EDGE,"E49"),sQuery(id+"F36.wireOp",EDGE,"E50"),sQuery(id+"F36.wireOp",EDGE,"E51"),sQuery(id+"F36.wireOp",EDGE,"E52"),sQuery(id+"F36.wireOp",EDGE,"E53")])]});
            var Q17;
            Q17=makeQuery(id+"F39.opPattern","COPY",BODY,{"derivedFrom":makeQuery(id+"F37.opExtrude","SWEPT_BODY",BODY,{"disambiguationData":[OSD([sQuery(id+"F36.wireOp",EDGE,"E49"),sQuery(id+"F36.wireOp",EDGE,"E50"),sQuery(id+"F36.wireOp",EDGE,"E51"),sQuery(id+"F36.wireOp",EDGE,"E52"),sQuery(id+"F36.wireOp",EDGE,"E53")])]}),"instanceName":"1"});
            var Q18;
            Q18=makeQuery(id+"F43.opExtrude","SWEPT_BODY",BODY,{"disambiguationData":[OSD([sQuery(id+"F42.wireOp",EDGE,"E54"),sQuery(id+"F42.wireOp",EDGE,"E55"),sQuery(id+"F42.wireOp",EDGE,"E56"),sQuery(id+"F42.wireOp",EDGE,"E57"),sQuery(id+"F42.wireOp",EDGE,"E58")])]});
            var Q19;
            Q19=makeQuery(id+"F45.opPattern","COPY",BODY,{"derivedFrom":makeQuery(id+"F43.opExtrude","SWEPT_BODY",BODY,{"disambiguationData":[OSD([sQuery(id+"F42.wireOp",EDGE,"E54"),sQuery(id+"F42.wireOp",EDGE,"E55"),sQuery(id+"F42.wireOp",EDGE,"E56"),sQuery(id+"F42.wireOp",EDGE,"E57"),sQuery(id+"F42.wireOp",EDGE,"E58")])]}),"instanceName":"1"});
            deleteBodies(context, id + "F46", {"entities" : qUnion([Q0, Q1, Q2, Q3, Q4, Q5, Q6, Q7, Q8, Q9, Q10, Q11, Q12, Q13, Q14, Q15, Q16, Q17, Q18, Q19])});
        }
    });
